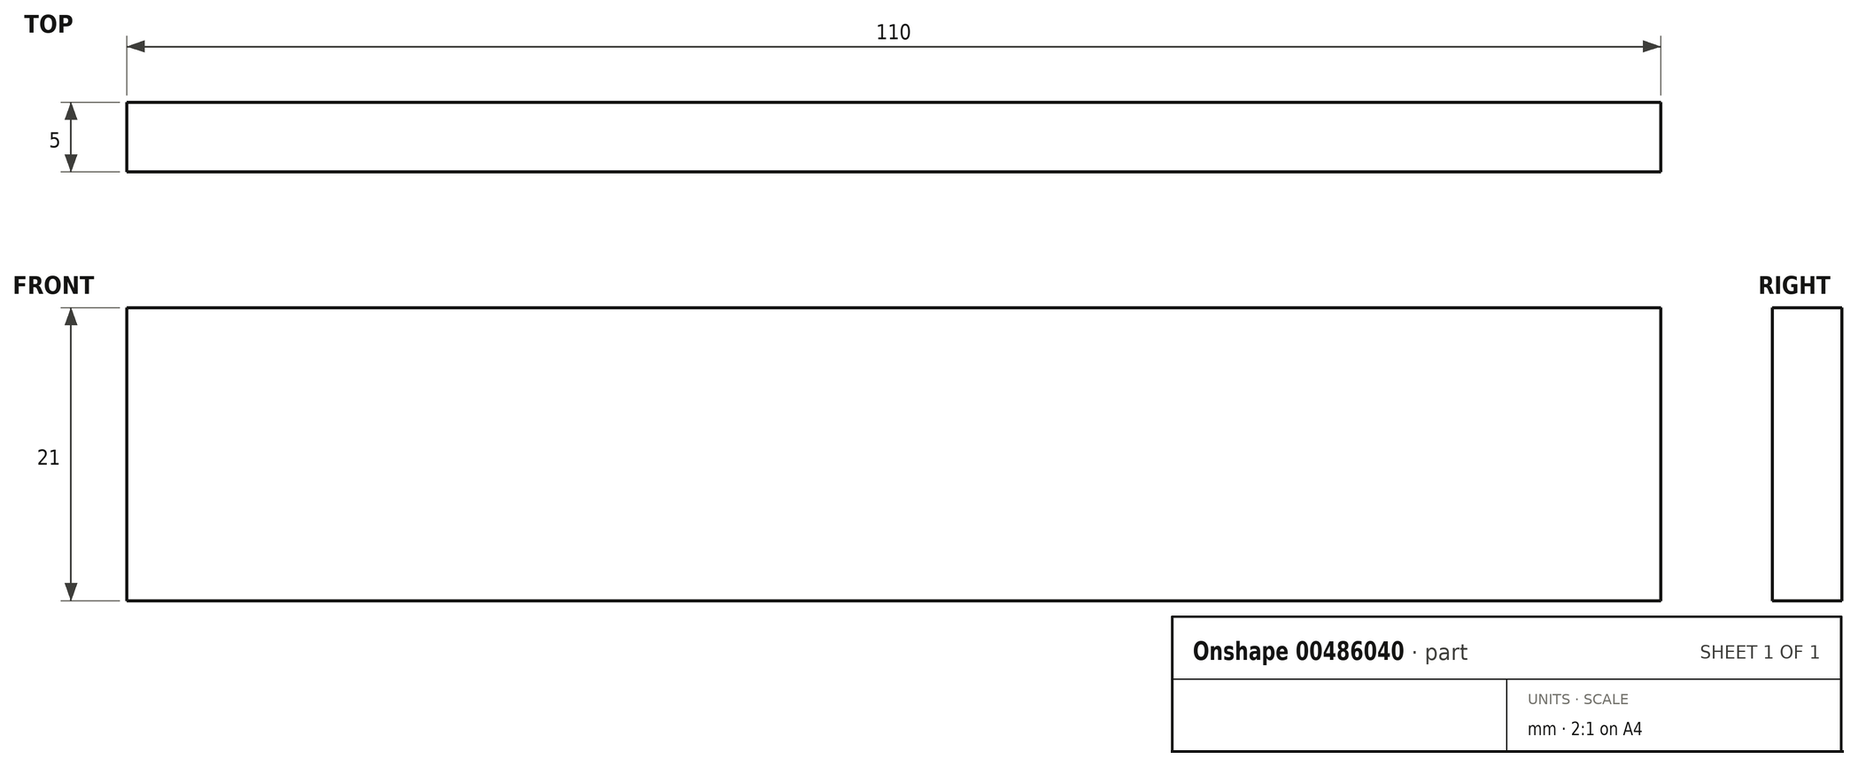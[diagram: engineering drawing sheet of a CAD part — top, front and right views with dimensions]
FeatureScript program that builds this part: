
annotation { "Feature Type Name" : "Feature", "Feature Type Description" : "" }
export const myFeature = defineFeature(function(context is Context, id is Id, definition is map)
    precondition{}
    {
        {
            var Q0;
            Q0=qCreatedBy(makeId("Front.planeOp"),FACE);
            var sketch = newSketch(context, id + "F0", { "sketchPlane" : qUnion([Q0])});
            skLineSegment(sketch, "E0.bottom", {"start": v(55, 10.5) * mm, "end": v(-55, 10.5) * mm});
            skLineSegment(sketch, "E0.top", {"start": v(55, -10.5) * mm, "end": v(-55, -10.5) * mm});
            skLineSegment(sketch, "E0.left", {"start": v(55, 10.5) * mm, "end": v(55, -10.5) * mm});
            skLineSegment(sketch, "E0.right", {"start": v(-55, 10.5) * mm, "end": v(-55, -10.5) * mm});
            skPoint(sketch, "E0.middle", {"position": v(0, 0) * mm});
            skSolve(sketch);
        }
        {
            var Q0;
            Q0=makeQuery(id+"F0.imprint","IMPRINT",FACE,{"disambiguationData":[TD([[makeQuery(id+"F0.imprint","IMPRINT",EDGE,{"derivedFrom":sQuery(id+"F0.wireOp",EDGE,"E0.bottom")}),1.0]])]});
            extrude(context, id + "F1", {"entities" : qUnion([Q0]), "depth" : 5 * mm});
        }
    });
